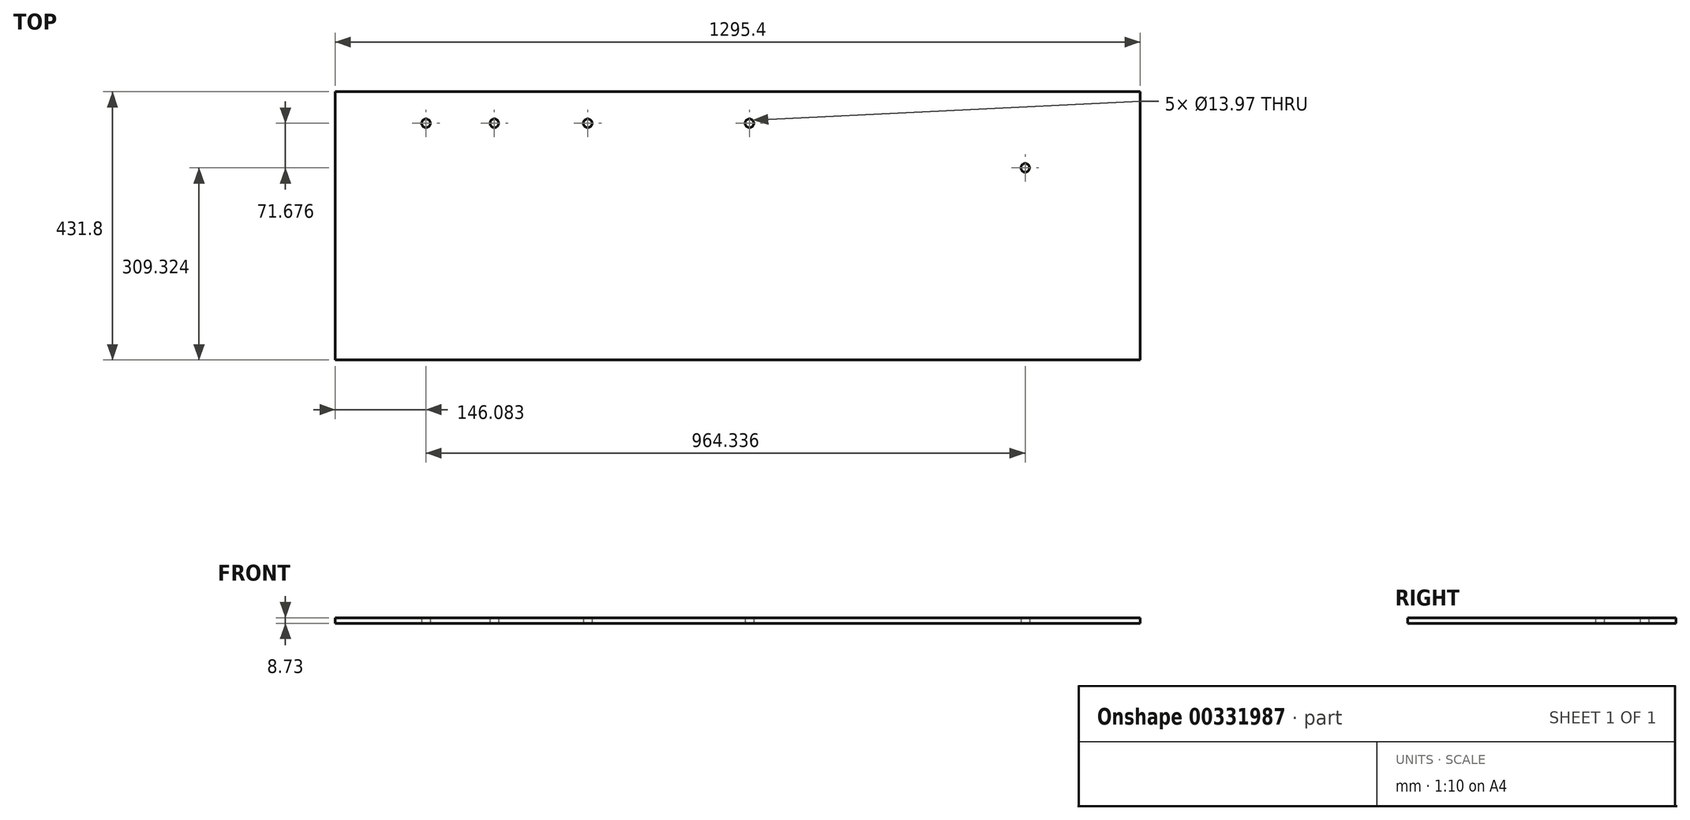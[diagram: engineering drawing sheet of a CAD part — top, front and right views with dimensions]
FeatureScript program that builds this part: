
annotation { "Feature Type Name" : "Feature", "Feature Type Description" : "" }
export const myFeature = defineFeature(function(context is Context, id is Id, definition is map)
    precondition{}
    {
        {
            var Q0;
            Q0=qCreatedBy(makeId("Top.planeOp"),FACE);
            var sketch = newSketch(context, id + "F0", { "sketchPlane" : qUnion([Q0])});
            skLineSegment(sketch, "E0.bottom", {"start": v(647.7, -190.5) * mm, "end": v(-647.7, -190.5) * mm});
            skLineSegment(sketch, "E0.left", {"start": v(647.7, -190.5) * mm, "end": v(647.7, 190.5) * mm});
            skLineSegment(sketch, "E0.right", {"start": v(-647.7, -190.5) * mm, "end": v(-647.7, 190.5) * mm});
            skPoint(sketch, "E0.middle", {"position": v(0, 0) * mm});
            skLineSegment(sketch, "E1", {"start": v(-647.7, -165.1) * mm, "end": v(-596.9, -165.1) * mm});
            skLineSegment(sketch, "E2", {"start": v(-596.9, -165.1) * mm, "end": v(-596.9, -190.5) * mm});
            skLineSegment(sketch, "E3", {"start": v(-596.9, -165.1) * mm, "end": v(-501.62, 190.5) * mm});
            skLineSegment(sketch, "E4", {"start": v(-596.9, -165.1) * mm, "end": v(-391.6, 190.5) * mm});
            skLineSegment(sketch, "E5", {"start": v(-596.9, -165.1) * mm, "end": v(-241.3, 190.5) * mm});
            skLineSegment(sketch, "E6", {"start": v(-596.9, -165.1) * mm, "end": v(19.02, 190.5) * mm});
            skLineSegment(sketch, "E7", {"start": v(-596.9, -165.1) * mm, "end": v(730.22, 190.5) * mm});
            skLineSegment(sketch, "E8", {"start": v(-647.7, 190.5) * mm, "end": v(-647.7, 241.3) * mm});
            skLineSegment(sketch, "E9", {"start": v(-647.7, 241.3) * mm, "end": v(647.7, 241.3) * mm});
            skLineSegment(sketch, "E10", {"start": v(647.7, 241.3) * mm, "end": v(647.7, 190.5) * mm});
            skCircle(sketch, "E11", {"center": v(-501.62, 190.5) * mm, "radius": 6.99 * mm});
            skCircle(sketch, "E12", {"center": v(-391.6, 190.5) * mm, "radius": 6.99 * mm});
            skCircle(sketch, "E13", {"center": v(-241.3, 190.5) * mm, "radius": 6.99 * mm});
            skCircle(sketch, "E14", {"center": v(19.02, 190.5) * mm, "radius": 6.99 * mm});
            skCircle(sketch, "E15", {"center": v(462.72, 118.82) * mm, "radius": 6.99 * mm});
            skSolve(sketch);
        }
        {
            var Q0;
            Q0 = qSketchRegion(id + "F0", true);
            extrude(context, id + "F1", {"entities" : qUnion([Q0]), "depth" : 8.73 * mm});
        }
    });
